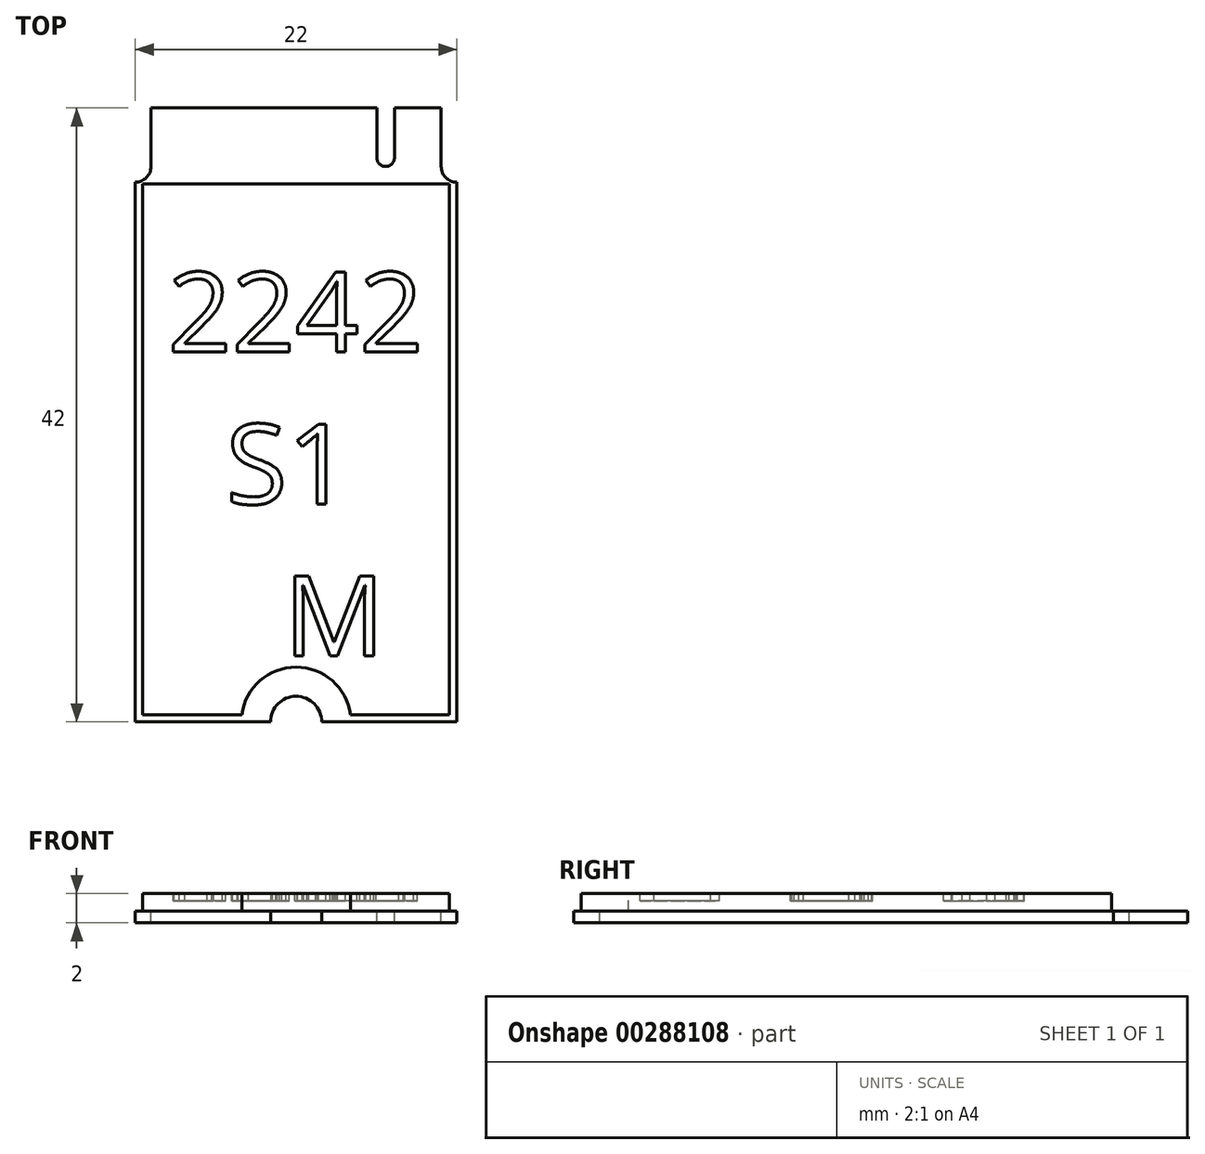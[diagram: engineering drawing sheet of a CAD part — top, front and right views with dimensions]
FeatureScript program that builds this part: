
annotation { "Feature Type Name" : "Feature", "Feature Type Description" : "" }
export const myFeature = defineFeature(function(context is Context, id is Id, definition is map)
    precondition{}
    {
        {
            assignVariable(context, id + "F0", {"name" : "thick", "anyValue" : .8});
        }
        {
            assignVariable(context, id + "F1", {"name" : "compheight", "anyValue" : 1.2});
        }
        {
            var Q0;
            Q0=qCreatedBy(makeId("Top.planeOp"),FACE);
            var sketch = newSketch(context, id + "F2", { "sketchPlane" : qUnion([Q0])});
            skLineSegment(sketch, "E0.bottom", {"start": v(-11, 21) * mm, "end": v(11, 21) * mm});
            skLineSegment(sketch, "E0.top", {"start": v(-11, -21) * mm, "end": v(11, -21) * mm});
            skLineSegment(sketch, "E0.left", {"start": v(-11, 21) * mm, "end": v(-11, -21) * mm});
            skLineSegment(sketch, "E0.right", {"start": v(11, 21) * mm, "end": v(11, -21) * mm});
            skPoint(sketch, "E0.middle", {"position": v(0, 0) * mm});
            skSolve(sketch);
        }
        {
            var Q0;
            Q0=qSketchRegion(id+"F2",true);
            extrude(context, id + "F3", {"entities" : qUnion([Q0]), "depth" : (getVariable(context, 'thick')) * mm});
        }
        {
            var Q0;
            Q0=makeQuery(id+"F3.opExtrude","CAP_FACE",FACE,{"disambiguationData":[OSD([sQuery(id+"F2.wireOp",EDGE,"E0.bottom"),sQuery(id+"F2.wireOp",EDGE,"E0.top"),sQuery(id+"F2.wireOp",EDGE,"E0.left"),sQuery(id+"F2.wireOp",EDGE,"E0.right")])],"isStart":false});
            var sketch = newSketch(context, id + "F4", { "sketchPlane" : qUnion([Q0])});
            skLineSegment(sketch, "E1.bottom", {"start": v(-10.5, -20.5) * mm, "end": v(10.5, -20.5) * mm});
            skLineSegment(sketch, "E1.top", {"start": v(-10.5, 15.8) * mm, "end": v(10.5, 15.8) * mm});
            skLineSegment(sketch, "E1.left", {"start": v(-10.5, -20.5) * mm, "end": v(-10.5, 15.8) * mm});
            skLineSegment(sketch, "E1.right", {"start": v(10.5, -20.5) * mm, "end": v(10.5, 15.8) * mm});
            skLineSegment(sketch, "E2", {"start": v(0, -21) * mm, "end": v(0, -20.5) * mm, "construction": true});
            skLineSegment(sketch, "E3", {"start": v(10.5, -2.35) * mm, "end": v(11, -2.35) * mm, "construction": true});
            skLineSegment(sketch, "E4", {"start": v(0, 15.8) * mm, "end": v(0, 21) * mm, "construction": true});
            skSolve(sketch);
        }
        {
            var Q0;
            Q0=qSketchRegion(id+"F4",true);
            extrude(context, id + "F5", {"entities" : qUnion([Q0]), "operationType" : NewBodyOperationType.ADD, "depth" : (getVariable(context, 'compheight')) * mm});
        }
        {
            var Q0;
            Q0=makeQuery(id+"F3.opExtrude","CAP_FACE",FACE,{"disambiguationData":[OSD([sQuery(id+"F2.wireOp",EDGE,"E0.bottom"),sQuery(id+"F2.wireOp",EDGE,"E0.top"),sQuery(id+"F2.wireOp",EDGE,"E0.left"),sQuery(id+"F2.wireOp",EDGE,"E0.right")])],"isStart":false});
            var sketch = newSketch(context, id + "F6", { "sketchPlane" : qUnion([Q0])});
            skLineSegment(sketch, "E5", {"start": v(0, 21) * mm, "end": v(0, 15.8) * mm, "construction": true});
            skLineSegment(sketch, "E6", {"start": v(-9.92, 21) * mm, "end": v(-9.92, 17) * mm});
            skArc(sketch, "E7", {"start": v(-11, 15.93) * mm, "mid": v(-10.24, 16.24) * mm, "end": v(-9.93, 17) * mm});
            skLineSegment(sketch, "E8", {"start": v(-9.92, 21) * mm, "end": v(-11, 21) * mm});
            skLineSegment(sketch, "E9", {"start": v(-11, 21) * mm, "end": v(-11, 15.92) * mm});
            skLineSegment(sketch, "E10.MirrorCS", {"start": v(9.93, 21) * mm, "end": v(9.93, 17) * mm});
            skLineSegment(sketch, "E11.MirrorCS", {"start": v(9.92, 21) * mm, "end": v(11, 21) * mm});
            skLineSegment(sketch, "E12.MirrorCS", {"start": v(11, 21) * mm, "end": v(11, 15.92) * mm});
            skArc(sketch, "E13.MirrorCS", {"start": v(11, 15.93) * mm, "mid": v(10.24, 16.24) * mm, "end": v(9.93, 17) * mm});
            skLineSegment(sketch, "E14", {"start": v(-9.92, 21) * mm, "end": v(9.92, 21) * mm, "construction": true});
            skLineSegment(sketch, "E15", {"start": v(0, 21) * mm, "end": v(6.13, 21) * mm, "construction": true});
            skLineSegment(sketch, "E16", {"start": v(6.13, 21) * mm, "end": v(6.13, 17.6) * mm, "construction": true});
            skLineSegment(sketch, "E17", {"start": v(0, 21) * mm, "end": v(-5.63, 21) * mm, "construction": true});
            skLineSegment(sketch, "E18", {"start": v(-9.92, 17) * mm, "end": v(6.13, 17) * mm, "construction": true});
            skArc(sketch, "E19", {"start": v(5.53, 17.6) * mm, "mid": v(6.13, 17) * mm, "end": v(6.73, 17.6) * mm});
            skLineSegment(sketch, "E20", {"start": v(6.13, 17.6) * mm, "end": v(5.53, 17.6) * mm, "construction": true});
            skLineSegment(sketch, "E21", {"start": v(6.73, 17.6) * mm, "end": v(6.73, 21) * mm});
            skLineSegment(sketch, "E22", {"start": v(6.73, 21) * mm, "end": v(5.53, 21) * mm});
            skLineSegment(sketch, "E23", {"start": v(5.53, 21) * mm, "end": v(5.53, 17.6) * mm});
            skLineSegment(sketch, "E24", {"start": v(-6.23, 26.62) * mm, "end": v(-6.23, 21) * mm, "construction": true});
            skLineSegment(sketch, "E25", {"start": v(-5.03, 26.62) * mm, "end": v(-5.03, 21) * mm, "construction": true});
            skArc(sketch, "E26", {"start": v(-6.23, 26.62) * mm, "mid": v(-5.63, 26.02) * mm, "end": v(-5.03, 26.62) * mm, "construction": true});
            skLineSegment(sketch, "E27", {"start": v(-6.23, 26.62) * mm, "end": v(-5.03, 26.62) * mm, "construction": true});
            skLineSegment(sketch, "E28", {"start": v(-5.63, 26.62) * mm, "end": v(-5.63, 21) * mm, "construction": true});
            skLineSegment(sketch, "E29", {"start": v(-6.23, 21) * mm, "end": v(-5.03, 21) * mm});
            skSolve(sketch);
        }
        {
            var Q0;
            Q0=qSketchRegion(id+"F6",true);
            extrude(context, id + "F7", {"entities" : qUnion([Q0]), "operationType" : NewBodyOperationType.REMOVE, "endBound" : BoundingType.THROUGH_ALL, "oppositeDirection" : true, "depth" : 25 * mm});
        }
        {
            var Q0;
            Q0=makeQuery(id+"F3.opExtrude","CAP_FACE",FACE,{"disambiguationData":[OSD([sQuery(id+"F2.wireOp",EDGE,"E0.bottom"),sQuery(id+"F2.wireOp",EDGE,"E0.top"),sQuery(id+"F2.wireOp",EDGE,"E0.left"),sQuery(id+"F2.wireOp",EDGE,"E0.right")])],"isStart":true});
            var sketch = newSketch(context, id + "F8", { "sketchPlane" : qUnion([Q0])});
            skCircle(sketch, "E30", {"center": v(0, 21) * mm, "radius": 1.75 * mm});
            skSolve(sketch);
        }
        {
            var Q0;
            Q0=qSketchRegion(id+"F8",true);
            extrude(context, id + "F9", {"entities" : qUnion([Q0]), "operationType" : NewBodyOperationType.REMOVE, "endBound" : BoundingType.THROUGH_ALL, "oppositeDirection" : true, "depth" : 25 * mm});
        }
        {
            var Q0;
            Q0=makeQuery(id+"F5.opExtrude","CAP_FACE",FACE,{"disambiguationData":[OSD([sQuery(id+"F4.wireOp",EDGE,"E1.bottom"),sQuery(id+"F4.wireOp",EDGE,"E1.top"),sQuery(id+"F4.wireOp",EDGE,"E1.left"),sQuery(id+"F4.wireOp",EDGE,"E1.right")])],"isStart":false});
            var sketch = newSketch(context, id + "F10", { "sketchPlane" : qUnion([Q0])});
            skArc(sketch, "E31.0", {"start": v(1.68, -20.5) * mm, "mid": v(0, -19.25) * mm, "end": v(-1.68, -20.5) * mm});
            skArc(sketch, "E32.0", {"start": v(3.72, -20.5) * mm, "mid": v(0, -17.25) * mm, "end": v(-3.72, -20.5) * mm});
            skLineSegment(sketch, "E33", {"start": v(-1.68, -20.5) * mm, "end": v(-3.72, -20.5) * mm});
            skLineSegment(sketch, "E34", {"start": v(1.68, -20.5) * mm, "end": v(3.72, -20.5) * mm});
            skSolve(sketch);
        }
        {
            var Q0;
            Q0=qSketchRegion(id+"F10",true);
            var Q1;
            Q1=makeQuery(id+"F3.opExtrude","CAP_FACE",FACE,{"disambiguationData":[OSD([sQuery(id+"F2.wireOp",EDGE,"E0.bottom"),sQuery(id+"F2.wireOp",EDGE,"E0.top"),sQuery(id+"F2.wireOp",EDGE,"E0.left"),sQuery(id+"F2.wireOp",EDGE,"E0.right")])],"isStart":false});
            extrude(context, id + "F11", {"entities" : qUnion([Q0]), "operationType" : NewBodyOperationType.REMOVE, "endBound" : BoundingType.UP_TO_SURFACE, "oppositeDirection" : true, "endBoundEntityFace" : qUnion([Q1]), "depth" : 25 * mm});
        }
        {
            var Q0;
            Q0=makeQuery(id+"F5.opExtrude","CAP_FACE",FACE,{"disambiguationData":[OSD([sQuery(id+"F4.wireOp",EDGE,"E1.bottom"),sQuery(id+"F4.wireOp",EDGE,"E1.top"),sQuery(id+"F4.wireOp",EDGE,"E1.left"),sQuery(id+"F4.wireOp",EDGE,"E1.right")])],"isStart":false});
            var sketch = newSketch(context, id + "F12", { "sketchPlane" : qUnion([Q0])});
            skText(sketch, "E35", { "text": "2242\n  S1\n    M", "fontName": "OpenSans-Regular.ttf"});
            skLineSegment(sketch, "E36", {"start": v(0, 15.8) * mm, "end": v(0, 9.8) * mm, "construction": true});
            const initialGuessF12  = {"E35": [-0.00878, 0.0043, 1, 0, 0.0055]};
            skSetInitialGuess(sketch, initialGuessF12);
            skSolve(sketch);
        }
        {
            var Q0;
            Q0=qSketchRegion(id+"F12",true);
            extrude(context, id + "F13", {"entities" : qUnion([Q0]), "operationType" : NewBodyOperationType.REMOVE, "oppositeDirection" : true, "depth" : .5 * mm});
        }
    });
